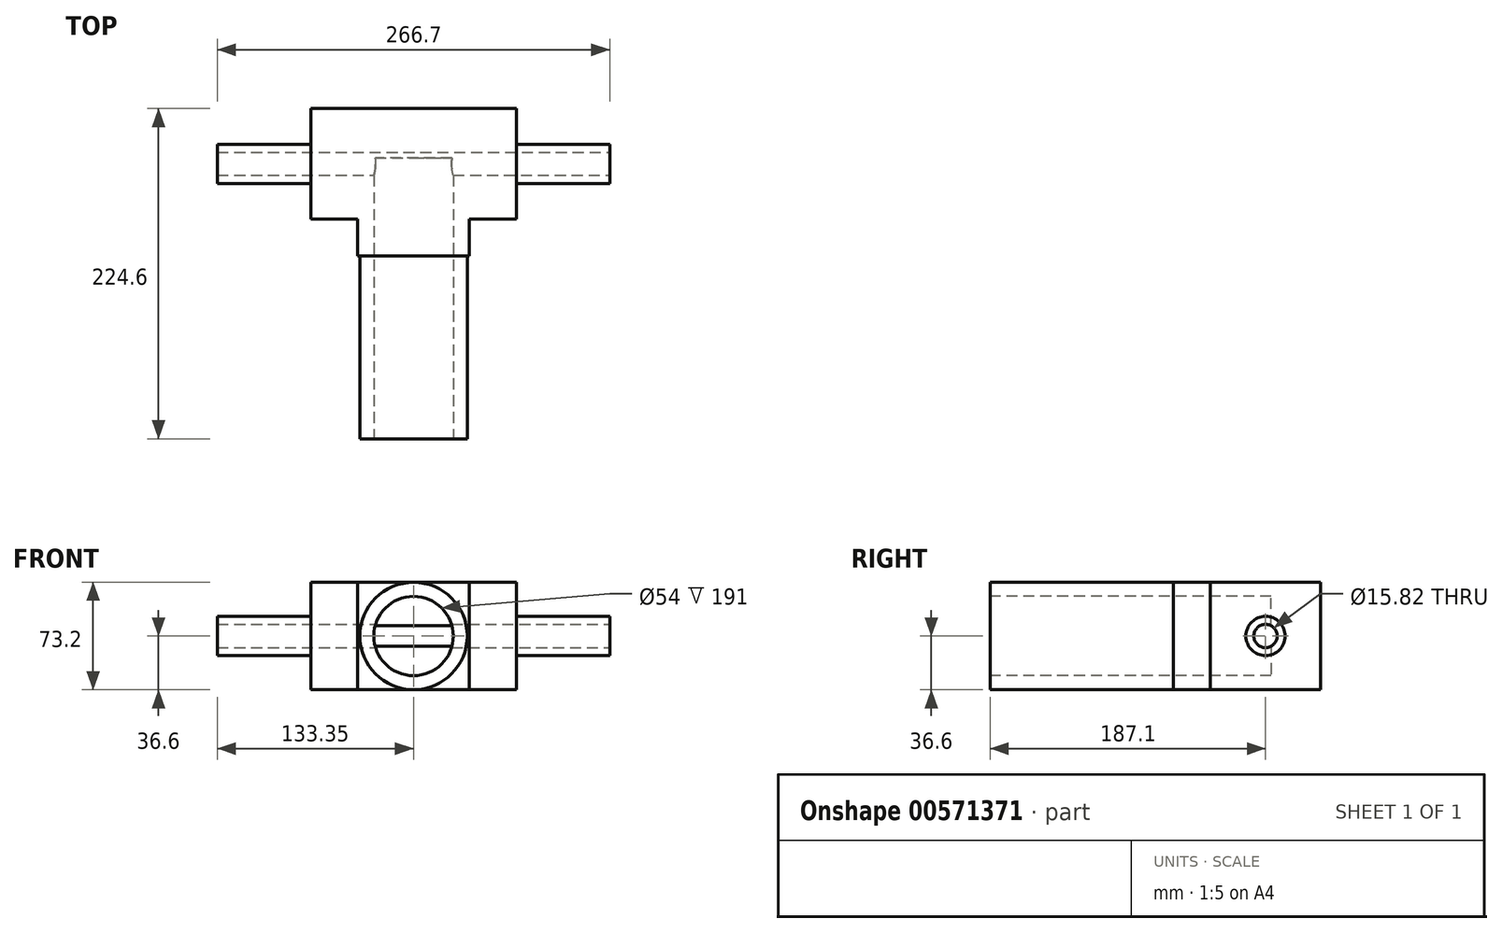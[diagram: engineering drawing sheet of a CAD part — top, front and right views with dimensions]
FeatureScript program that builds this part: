
annotation { "Feature Type Name" : "Feature", "Feature Type Description" : "" }
export const myFeature = defineFeature(function(context is Context, id is Id, definition is map)
    precondition{}
    {
        {
            var Q0;
            Q0=qCreatedBy(makeId("Front.planeOp"),FACE);
            var sketch = newSketch(context, id + "F0", { "sketchPlane" : qUnion([Q0])});
            skLineSegment(sketch, "E0.bottom", {"start": v(-133.35, -36.6) * mm, "end": v(133.35, -36.6) * mm});
            skLineSegment(sketch, "E0.top", {"start": v(-133.35, 36.6) * mm, "end": v(133.35, 36.6) * mm});
            skLineSegment(sketch, "E0.left", {"start": v(-133.35, -36.6) * mm, "end": v(-133.35, 36.6) * mm});
            skLineSegment(sketch, "E0.right", {"start": v(133.35, -36.6) * mm, "end": v(133.35, 36.6) * mm});
            skPoint(sketch, "E0.middle", {"position": v(0, 0) * mm});
            skSolve(sketch);
        }
        {
            var Q0;
            Q0 = qSketchRegion(id + "F0", true);
            extrude(context, id + "F1", {"entities" : qUnion([Q0]), "depth" : 75 * mm, "offsetDistance" : 25 * mm});
        }
        {
            var Q0;
            Q0=makeQuery(id+"F1.opExtrude","CAP_FACE",FACE,{"disambiguationData":[OSD([sQuery(id+"F0.wireOp",EDGE,"E0.bottom"),sQuery(id+"F0.wireOp",EDGE,"E0.top"),sQuery(id+"F0.wireOp",EDGE,"E0.left"),sQuery(id+"F0.wireOp",EDGE,"E0.right")])],"isStart":false});
            var sketch = newSketch(context, id + "F2", { "sketchPlane" : qUnion([Q0])});
            skLineSegment(sketch, "E1.bottom", {"start": v(-38, -36.6) * mm, "end": v(38, -36.6) * mm});
            skLineSegment(sketch, "E1.top", {"start": v(-38, 36.6) * mm, "end": v(38, 36.6) * mm});
            skLineSegment(sketch, "E1.left", {"start": v(-38, -36.6) * mm, "end": v(-38, 36.6) * mm});
            skLineSegment(sketch, "E1.right", {"start": v(38, -36.6) * mm, "end": v(38, 36.6) * mm});
            skPoint(sketch, "E1.middle", {"position": v(0, 0) * mm});
            skSolve(sketch);
        }
        {
            var Q0;
            Q0 = qSketchRegion(id + "F2", true);
            extrude(context, id + "F3", {"entities" : qUnion([Q0]), "operationType" : NewBodyOperationType.ADD, "depth" : 124.6 * mm, "offsetDistance" : 25 * mm});
        }
        {
            var Q0;
            Q0=makeQuery(id+"F1.opExtrude","SWEPT_FACE",FACE,{"disambiguationData":[OSD([sQuery(id+"F0.wireOp",EDGE,"E0.right")])]});
            var sketch = newSketch(context, id + "F4", { "sketchPlane" : qUnion([Q0])});
            skLineSegment(sketch, "E2", {"start": v(0, 0) * mm, "end": v(-75, 0) * mm});
            skCircle(sketch, "E3", {"center": v(-37.5, 0) * mm, "radius": 13.34 * mm});
            skCircle(sketch, "E4", {"center": v(-37.5, 0) * mm, "radius": 58.83 * mm});
            skSolve(sketch);
        }
        {
            var Q0;
            Q0 = qSketchRegion(id + "F4", true);
            extrude(context, id + "F5", {"entities" : qUnion([Q0]), "operationType" : NewBodyOperationType.REMOVE, "oppositeDirection" : true, "depth" : 63.5 * mm, "offsetDistance" : 25 * mm});
        }
        {
            var Q0;
            Q0=makeQuery(id+"F1.opExtrude","SWEPT_FACE",FACE,{"disambiguationData":[OSD([sQuery(id+"F0.wireOp",EDGE,"E0.left")])]});
            var sketch = newSketch(context, id + "F6", { "sketchPlane" : qUnion([Q0])});
            skLineSegment(sketch, "E5", {"start": v(0, 0) * mm, "end": v(75, 0) * mm});
            skCircle(sketch, "E6", {"center": v(37.5, 0) * mm, "radius": 13.34 * mm});
            skCircle(sketch, "E7", {"center": v(37.5, 0) * mm, "radius": 62.87 * mm});
            skSolve(sketch);
        }
        {
            var Q0;
            Q0 = qSketchRegion(id + "F6", true);
            extrude(context, id + "F7", {"entities" : qUnion([Q0]), "operationType" : NewBodyOperationType.REMOVE, "oppositeDirection" : true, "depth" : 63.5 * mm, "offsetDistance" : 25 * mm});
        }
        {
            var Q0;
            Q0=makeQuery(id+"F3.opExtrude","CAP_FACE",FACE,{"disambiguationData":[OSD([sQuery(id+"F2.wireOp",EDGE,"E1.bottom"),sQuery(id+"F2.wireOp",EDGE,"E1.top"),sQuery(id+"F2.wireOp",EDGE,"E1.left"),sQuery(id+"F2.wireOp",EDGE,"E1.right")])],"isStart":false});
            extrude(context, id + "F8", {"entities" : qUnion([Q0]), "operationType" : NewBodyOperationType.ADD, "depth" : 25 * mm, "offsetDistance" : 25 * mm});
        }
        {
            var Q0;
            Q0=makeQuery(id+"F8.opExtrude","CAP_FACE",FACE,{"disambiguationData":[OSD([sQuery(id+"F2.wireOp",EDGE,"E1.bottom"),sQuery(id+"F2.wireOp",EDGE,"E1.top"),sQuery(id+"F2.wireOp",EDGE,"E1.left"),sQuery(id+"F2.wireOp",EDGE,"E1.right")])],"isStart":false});
            var sketch = newSketch(context, id + "F9", { "sketchPlane" : qUnion([Q0])});
            skCircle(sketch, "E8", {"center": v(0, 0) * mm, "radius": 36.5 * mm});
            skCircle(sketch, "E9", {"center": v(0, 0) * mm, "radius": 76.9 * mm});
            skSolve(sketch);
        }
        {
            var Q0;
            Q0 = qSketchRegion(id + "F9", true);
            extrude(context, id + "F10", {"entities" : qUnion([Q0]), "operationType" : NewBodyOperationType.REMOVE, "oppositeDirection" : true, "depth" : 124.5 * mm, "offsetDistance" : 25 * mm});
        }
        {
            var Q0;
            Q0=makeQuery(id+"F8.opExtrude","CAP_FACE",FACE,{"disambiguationData":[OSD([sQuery(id+"F2.wireOp",EDGE,"E1.bottom"),sQuery(id+"F2.wireOp",EDGE,"E1.top"),sQuery(id+"F2.wireOp",EDGE,"E1.left"),sQuery(id+"F2.wireOp",EDGE,"E1.right")])],"isStart":false});
            var sketch = newSketch(context, id + "F11", { "sketchPlane" : qUnion([Q0])});
            skCircle(sketch, "E10", {"center": v(0, 0) * mm, "radius": 27 * mm});
            skSolve(sketch);
        }
        {
            var Q0;
            Q0 = qSketchRegion(id + "F11", true);
            extrude(context, id + "F12", {"entities" : qUnion([Q0]), "operationType" : NewBodyOperationType.REMOVE, "oppositeDirection" : true, "depth" : 191 * mm, "offsetDistance" : 25 * mm});
        }
        {
            var Q0;
            Q0=makeQuery(id+"F1.opExtrude","SWEPT_FACE",FACE,{"disambiguationData":[OSD([sQuery(id+"F0.wireOp",EDGE,"E0.right")])]});
            var sketch = newSketch(context, id + "F13", { "sketchPlane" : qUnion([Q0])});
            skCircle(sketch, "E11", {"center": v(-37.5, 0) * mm, "radius": 7.9 * mm});
            skSolve(sketch);
        }
        {
            var Q0;
            Q0 = qSketchRegion(id + "F13", true);
            extrude(context, id + "F14", {"entities" : qUnion([Q0]), "operationType" : NewBodyOperationType.REMOVE, "oppositeDirection" : true, "depth" : 291 * mm, "offsetDistance" : 25 * mm});
        }
    });
